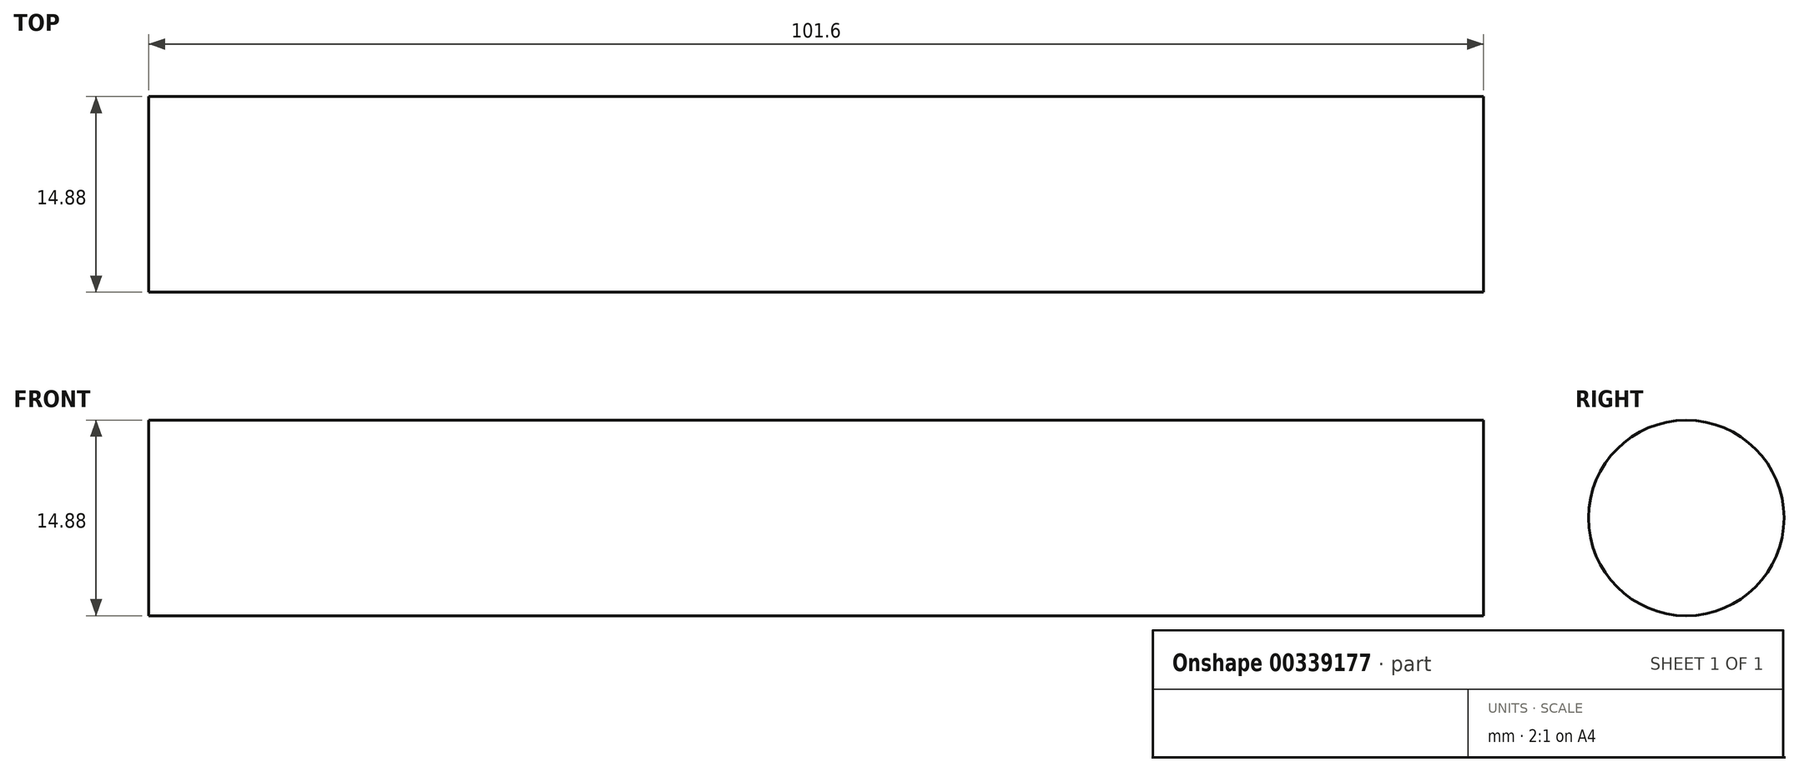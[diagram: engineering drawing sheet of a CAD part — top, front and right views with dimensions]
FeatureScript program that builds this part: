
annotation { "Feature Type Name" : "Feature", "Feature Type Description" : "" }
export const myFeature = defineFeature(function(context is Context, id is Id, definition is map)
    precondition{}
    {
        {
            var Q0;
            Q0=qCreatedBy(makeId("Right.planeOp"),FACE);
            var sketch = newSketch(context, id + "F0", { "sketchPlane" : qUnion([Q0])});
            skCircle(sketch, "E0", {"center": v(0, 0) * mm, "radius": 7.44 * mm});
            skSolve(sketch);
        }
        {
            var Q0;
            Q0 = qSketchRegion(id + "F0", true);
            extrude(context, id + "F1", {"entities" : qUnion([Q0]), "depth" : 101.6 * mm});
        }
    });
